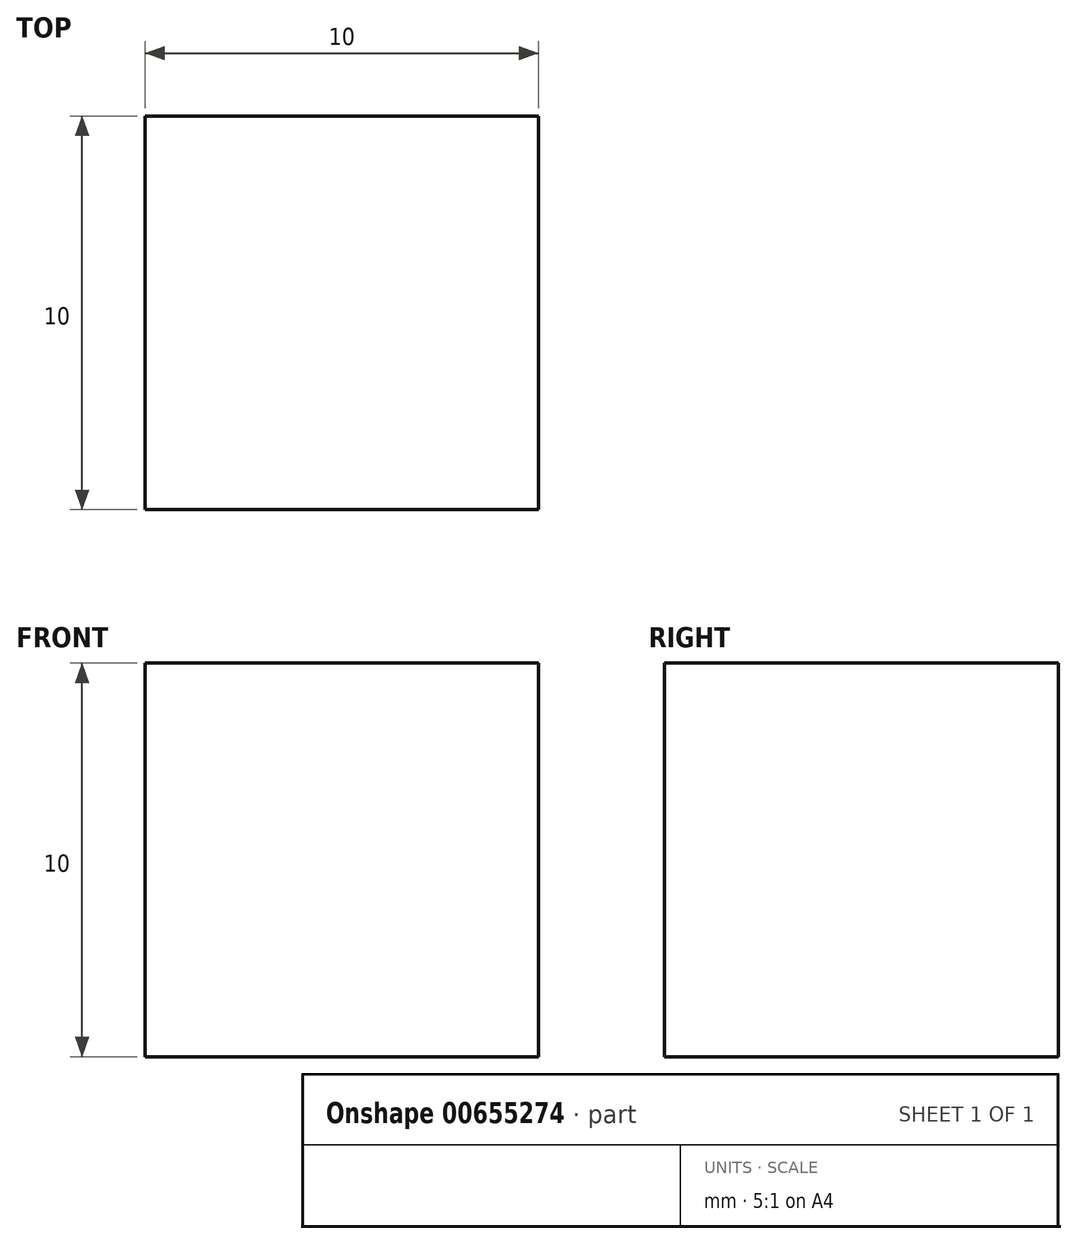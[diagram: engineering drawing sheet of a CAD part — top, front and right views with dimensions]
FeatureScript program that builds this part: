
annotation { "Feature Type Name" : "Feature", "Feature Type Description" : "" }
export const myFeature = defineFeature(function(context is Context, id is Id, definition is map)
    precondition{}
    {
        {
            var Q0;
            Q0=qCreatedBy(makeId("Top.planeOp"),FACE);
            var sketch = newSketch(context, id + "F0", { "sketchPlane" : qUnion([Q0])});
            skLineSegment(sketch, "E0.bottom", {"start": v(-5, 5) * mm, "end": v(5, 5) * mm});
            skLineSegment(sketch, "E0.top", {"start": v(-5, -5) * mm, "end": v(5, -5) * mm});
            skLineSegment(sketch, "E0.left", {"start": v(-5, 5) * mm, "end": v(-5, -5) * mm});
            skLineSegment(sketch, "E0.right", {"start": v(5, 5) * mm, "end": v(5, -5) * mm});
            skPoint(sketch, "E0.middle", {"position": v(0, 0) * mm});
            skSolve(sketch);
        }
        {
            var Q0;
            Q0 = qSketchRegion(id + "F0", true);
            extrude(context, id + "F1", {"entities" : qUnion([Q0]), "depth" : 10 * mm, "offsetDistance" : 25.4 * mm});
        }
    });
